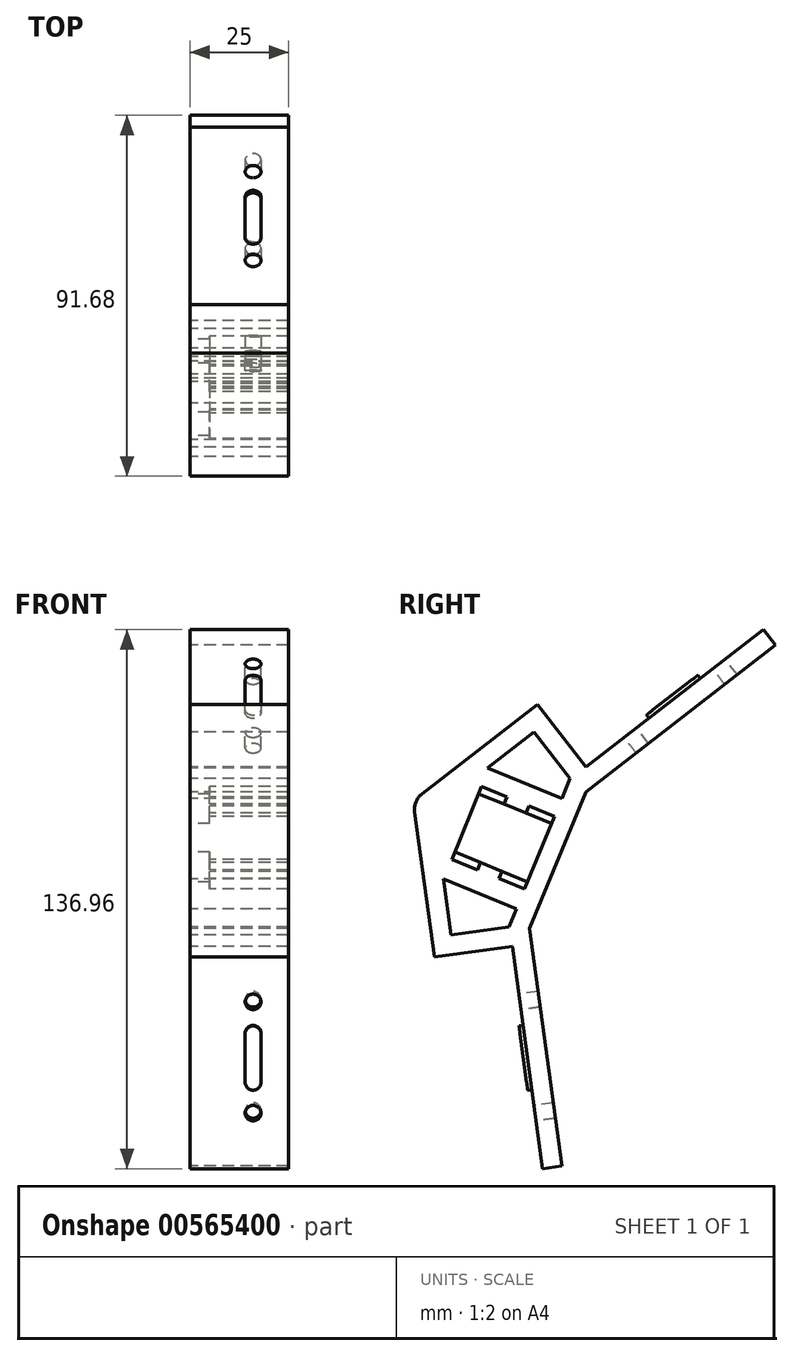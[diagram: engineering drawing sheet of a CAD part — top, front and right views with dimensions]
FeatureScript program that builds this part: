
annotation { "Feature Type Name" : "Feature", "Feature Type Description" : "" }
export const myFeature = defineFeature(function(context is Context, id is Id, definition is map)
    precondition{}
    {
        {
            var Q0;
            Q0=qCreatedBy(makeId("Right.planeOp"),FACE);
            var sketch = newSketch(context, id + "F0", { "sketchPlane" : qUnion([Q0])});
            skLineSegment(sketch, "E0", {"start": v(-33.6, 14.18) * mm, "end": v(-1.95, 38.65) * mm});
            skLineSegment(sketch, "E1", {"start": v(-1.95, 38.65) * mm, "end": v(10.28, 22.83) * mm});
            skLineSegment(sketch, "E2", {"start": v(-8.4, -22.77) * mm, "end": v(-28.23, -25.46) * mm});
            skLineSegment(sketch, "E3", {"start": v(-28.23, -25.46) * mm, "end": v(-33.6, 14.18) * mm});
            skLineSegment(sketch, "E4", {"start": v(10.28, 22.83) * mm, "end": v(55.37, 57.7) * mm});
            skLineSegment(sketch, "E5", {"start": v(55.37, 57.7) * mm, "end": v(58.43, 53.74) * mm});
            skLineSegment(sketch, "E6", {"start": v(58.43, 53.74) * mm, "end": v(10.28, 16.5) * mm});
            skLineSegment(sketch, "E7", {"start": v(10.28, 16.5) * mm, "end": v(-3.97, -18.27) * mm});
            skLineSegment(sketch, "E8", {"start": v(-3.97, -18.27) * mm, "end": v(4.2, -78.59) * mm});
            skLineSegment(sketch, "E9", {"start": v(4.2, -78.59) * mm, "end": v(-0.75, -79.26) * mm});
            skLineSegment(sketch, "E10", {"start": v(-0.75, -79.26) * mm, "end": v(-8.4, -22.77) * mm});
            skPoint(sketch, "E11", {"position": v(34.35, 35.12) * mm});
            skPoint(sketch, "E12", {"position": v(0.11, -48.43) * mm});
            skLineSegment(sketch, "E13", {"start": v(2.32, 10.27) * mm, "end": v(-16.19, 17.85) * mm});
            skLineSegment(sketch, "E14", {"start": v(-16.19, 17.85) * mm, "end": v(-23.77, -0.65) * mm});
            skLineSegment(sketch, "E15", {"start": v(-23.77, -0.65) * mm, "end": v(-5.26, -8.24) * mm});
            skLineSegment(sketch, "E16", {"start": v(-5.26, -8.24) * mm, "end": v(2.32, 10.27) * mm});
            skPoint(sketch, "E17", {"position": v(3.15, -0.88) * mm});
            skPoint(sketch, "E18", {"position": v(-1.47, 1.01) * mm});
            skLineSegment(sketch, "E19", {"start": v(3.15, -0.88) * mm, "end": v(-1.47, 1.01) * mm});
            skLineSegment(sketch, "E20", {"start": v(1.56, 8.42) * mm, "end": v(-16.94, 16) * mm});
            skLineSegment(sketch, "E21", {"start": v(-4.5, -6.39) * mm, "end": v(-23.01, 1.2) * mm});
            skLineSegment(sketch, "E22", {"start": v(-11.74, -5.58) * mm, "end": v(-10.98, -3.73) * mm});
            skLineSegment(sketch, "E23", {"start": v(-17.3, -3.3) * mm, "end": v(-16.53, -1.46) * mm});
            skLineSegment(sketch, "E24", {"start": v(-10.47, 13.35) * mm, "end": v(-9.7, 15.2) * mm});
            skPoint(sketch, "E25", {"position": v(-14.52, -4.45) * mm});
            skPoint(sketch, "E26", {"position": v(-6.93, 14.06) * mm});
            skLineSegment(sketch, "E27", {"start": v(-4.92, 11.07) * mm, "end": v(-4.16, 12.92) * mm});
            skLineSegment(sketch, "E28", {"start": v(-2.85, 31.63) * mm, "end": v(6.25, 19.86) * mm});
            skLineSegment(sketch, "E29", {"start": v(6.25, 19.86) * mm, "end": v(4.17, 14.8) * mm});
            skLineSegment(sketch, "E30", {"start": v(4.17, 14.8) * mm, "end": v(-14.65, 22.5) * mm});
            skLineSegment(sketch, "E31", {"start": v(-14.65, 22.5) * mm, "end": v(-2.85, 31.63) * mm});
            skLineSegment(sketch, "E32", {"start": v(-7.31, -13.24) * mm, "end": v(-9.2, -17.83) * mm});
            skLineSegment(sketch, "E33", {"start": v(-9.2, -17.83) * mm, "end": v(-23.94, -19.83) * mm});
            skLineSegment(sketch, "E34", {"start": v(-23.94, -19.83) * mm, "end": v(-25.87, -5.64) * mm});
            skPoint(sketch, "E34.endSnap0", {"position": v(-30.91, -5.64) * mm});
            skLineSegment(sketch, "E35", {"start": v(-25.87, -5.64) * mm, "end": v(-7.31, -13.24) * mm});
            skSolve(sketch);
        }
        {
            var Q0;
            Q0=makeQuery(id+"F0.imprint","IMPRINT",FACE,{"disambiguationData":[TD([[makeQuery(id+"F0.imprint","IMPRINT",EDGE,{"derivedFrom":sQuery(id+"F0.wireOp",EDGE,"E0")}),-1.0]])]});
            var Q1;
            {var subQ0=sQuery(id+"F0.wireOp",EDGE,"E22");Q1=makeQuery(id+"F0.imprint","IMPRINT",FACE,{"disambiguationData":[TD([[makeQuery(id+"F0.imprint","IMPRINT",EDGE,{"derivedFrom":subQ0}),1.0]])]});}
            var Q2;
            {var subQ0=sQuery(id+"F0.wireOp",EDGE,"E24");Q2=makeQuery(id+"F0.imprint","IMPRINT",FACE,{"disambiguationData":[TD([[makeQuery(id+"F0.imprint","IMPRINT",EDGE,{"derivedFrom":subQ0}),-1.0]])]});}
            extrude(context, id + "F1", {"entities" : qUnion([Q0, Q1, Q2]), "depth" : 25 * mm, "offsetDistance" : 25 * mm});
        }
        {
            var Q0;
            {var subQ3=sQuery(id+"F0.wireOp",EDGE,"E22");Q0=makeQuery(id+"F0.imprint","IMPRINT",FACE,{"disambiguationData":[TD([[makeQuery(id+"F0.imprint","IMPRINT",EDGE,{"derivedFrom":subQ3}),-1.0]])]});}
            var Q1;
            {var subQ5=sQuery(id+"F0.wireOp",EDGE,"E23");Q1=makeQuery(id+"F0.imprint","IMPRINT",FACE,{"disambiguationData":[TD([[makeQuery(id+"F0.imprint","IMPRINT",EDGE,{"derivedFrom":subQ5}),1.0]])]});}
            var Q2;
            {var subQ3=sQuery(id+"F0.wireOp",EDGE,"E24");Q2=makeQuery(id+"F0.imprint","IMPRINT",FACE,{"disambiguationData":[TD([[makeQuery(id+"F0.imprint","IMPRINT",EDGE,{"derivedFrom":subQ3}),1.0]])]});}
            var Q3;
            {var subQ3=sQuery(id+"F0.wireOp",EDGE,"E27");Q3=makeQuery(id+"F0.imprint","IMPRINT",FACE,{"disambiguationData":[TD([[makeQuery(id+"F0.imprint","IMPRINT",EDGE,{"derivedFrom":subQ3}),-1.0]])]});}
            extrude(context, id + "F2", {"entities" : qUnion([Q0, Q1, Q2, Q3]), "operationType" : NewBodyOperationType.ADD, "depth" : 5 * mm, "offsetDistance" : 25 * mm});
        }
        {
            var Q0;
            Q0=makeQuery(id+"F1.opExtrude","SWEPT_EDGE",EDGE,{"disambiguationData":[OSD([sQuery(id+"F0.wireOp",EDGE,"E0"),sQuery(id+"F0.wireOp",EDGE,"E3")])]});
            fillet(context, id + "F3", {"entities" : qUnion([Q0]), "radius" : 5 * mm, "tangentPropagation" : true, "allowEdgeOverflow" : false});
        }
        {
            var Q0;
            Q0=makeQuery(id+"F1.opExtrude","SWEPT_FACE",FACE,{"disambiguationData":[OSD([sQuery(id+"F0.wireOp",EDGE,"E4")])]});
            var sketch = newSketch(context, id + "F4", { "sketchPlane" : qUnion([Q0])});
            skCircle(sketch, "E36", {"center": v(16, 56.85) * mm, "radius": 2 * mm});
            skCircle(sketch, "E37", {"center": v(16, 44.35) * mm, "radius": 2 * mm});
            skLineSegment(sketch, "E38", {"start": v(18, 56.85) * mm, "end": v(18, 44.35) * mm});
            skLineSegment(sketch, "E39", {"start": v(14, 44.35) * mm, "end": v(14, 56.85) * mm});
            skCircle(sketch, "E40", {"center": v(16, 64.85) * mm, "radius": 2 * mm});
            skCircle(sketch, "E41", {"center": v(16, 36.35) * mm, "radius": 2 * mm});
            skLineSegment(sketch, "E42", {"start": v(18, 56.85) * mm, "end": v(18, 64.85) * mm});
            skLineSegment(sketch, "E43", {"start": v(14, 64.85) * mm, "end": v(14, 56.85) * mm});
            skLineSegment(sketch, "E44", {"start": v(18, 44.35) * mm, "end": v(18, 36.35) * mm});
            skLineSegment(sketch, "E45", {"start": v(14, 44.35) * mm, "end": v(14, 36.35) * mm});
            skSolve(sketch);
        }
        {
            var Q0;
            {var subQ0=sQuery(id+"F4.wireOp",EDGE,"E36");var subQ1=makeQuery(id+"F4.imprint","INTERSECT",VERTEX,{"derivedFrom":[subQ0,sQuery(id+"F4.wireOp",EDGE,"E38")]});Q0=makeQuery(id+"F4.imprint","IMPRINT",FACE,{"disambiguationData":[TD([[makeQuery(id+"F4.imprint","IMPRINT",EDGE,{"disambiguationData":[TD([[subQ1,-1.0]])],"derivedFrom":subQ0}),1.0]])]});}
            var Q1;
            {var subQ0=sQuery(id+"F4.wireOp",EDGE,"E37");var subQ1=makeQuery(id+"F4.imprint","INTERSECT",VERTEX,{"derivedFrom":[subQ0,sQuery(id+"F4.wireOp",EDGE,"E38")]});Q1=makeQuery(id+"F4.imprint","IMPRINT",FACE,{"disambiguationData":[TD([[makeQuery(id+"F4.imprint","IMPRINT",EDGE,{"disambiguationData":[TD([[subQ1,1.0]])],"derivedFrom":subQ0}),1.0]])]});}
            var Q2;
            {var subQ0=sQuery(id+"F4.wireOp",EDGE,"E38");Q2=makeQuery(id+"F4.imprint","IMPRINT",FACE,{"disambiguationData":[TD([[makeQuery(id+"F4.imprint","IMPRINT",EDGE,{"derivedFrom":subQ0}),-1.0]])]});}
            extrude(context, id + "F5", {"entities" : qUnion([Q0, Q1, Q2]), "operationType" : NewBodyOperationType.ADD, "depth" : 1 * mm, "offsetDistance" : 25 * mm});
        }
        {
            var Q0;
            {var subQ0=sQuery(id+"F4.wireOp",EDGE,"E40");var subQ1=makeQuery(id+"F4.imprint","INTERSECT",VERTEX,{"derivedFrom":[subQ0,sQuery(id+"F4.wireOp",EDGE,"E42")]});Q0=makeQuery(id+"F4.imprint","IMPRINT",FACE,{"disambiguationData":[TD([[makeQuery(id+"F4.imprint","IMPRINT",EDGE,{"disambiguationData":[TD([[subQ1,-1.0]])],"derivedFrom":subQ0}),1.0]])]});}
            var Q1;
            {var subQ0=sQuery(id+"F4.wireOp",EDGE,"E41");var subQ1=makeQuery(id+"F4.imprint","INTERSECT",VERTEX,{"derivedFrom":[subQ0,sQuery(id+"F4.wireOp",EDGE,"E44")]});Q1=makeQuery(id+"F4.imprint","IMPRINT",FACE,{"disambiguationData":[TD([[makeQuery(id+"F4.imprint","IMPRINT",EDGE,{"disambiguationData":[TD([[subQ1,-1.0]])],"derivedFrom":subQ0}),1.0]])]});}
            extrude(context, id + "F6", {"entities" : qUnion([Q0, Q1]), "operationType" : NewBodyOperationType.REMOVE, "oppositeDirection" : true, "depth" : 5 * mm, "offsetDistance" : 25 * mm});
        }
        {
            var Q0;
            Q0=makeQuery(id+"F1.opExtrude","SWEPT_FACE",FACE,{"disambiguationData":[OSD([sQuery(id+"F0.wireOp",EDGE,"E10")])]});
            var sketch = newSketch(context, id + "F7", { "sketchPlane" : qUnion([Q0])});
            skCircle(sketch, "E46", {"center": v(16, -35.69) * mm, "radius": 2 * mm});
            skCircle(sketch, "E47", {"center": v(16, -43.69) * mm, "radius": 2 * mm});
            skCircle(sketch, "E48", {"center": v(16, -56.19) * mm, "radius": 2 * mm});
            skCircle(sketch, "E49", {"center": v(16, -64.19) * mm, "radius": 2 * mm});
            skLineSegment(sketch, "E50", {"start": v(18, -35.69) * mm, "end": v(18, -43.69) * mm});
            skLineSegment(sketch, "E51", {"start": v(18, -43.69) * mm, "end": v(18, -56.19) * mm});
            skLineSegment(sketch, "E52", {"start": v(18, -64.19) * mm, "end": v(18, -56.19) * mm});
            skLineSegment(sketch, "E53", {"start": v(14, -35.69) * mm, "end": v(14, -43.69) * mm});
            skLineSegment(sketch, "E54", {"start": v(14, -43.69) * mm, "end": v(14, -56.19) * mm});
            skLineSegment(sketch, "E55", {"start": v(14, -56.19) * mm, "end": v(14, -64.19) * mm});
            skSolve(sketch);
        }
        {
            var Q0;
            {var subQ0=sQuery(id+"F7.wireOp",EDGE,"E47");var subQ1=makeQuery(id+"F7.imprint","INTERSECT",VERTEX,{"derivedFrom":[subQ0,sQuery(id+"F7.wireOp",EDGE,"E50"),sQuery(id+"F7.wireOp",EDGE,"E51")]});Q0=makeQuery(id+"F7.imprint","IMPRINT",FACE,{"disambiguationData":[TD([[makeQuery(id+"F7.imprint","IMPRINT",EDGE,{"disambiguationData":[TD([[subQ1,-1.0]])],"derivedFrom":subQ0}),1.0]])]});}
            var Q1;
            {var subQ0=sQuery(id+"F7.wireOp",EDGE,"E51");Q1=makeQuery(id+"F7.imprint","IMPRINT",FACE,{"disambiguationData":[TD([[makeQuery(id+"F7.imprint","IMPRINT",EDGE,{"derivedFrom":subQ0}),-1.0]])]});}
            var Q2;
            {var subQ0=sQuery(id+"F7.wireOp",EDGE,"E48");var subQ1=makeQuery(id+"F7.imprint","INTERSECT",VERTEX,{"derivedFrom":[subQ0,sQuery(id+"F7.wireOp",EDGE,"E51"),sQuery(id+"F7.wireOp",EDGE,"E52")]});Q2=makeQuery(id+"F7.imprint","IMPRINT",FACE,{"disambiguationData":[TD([[makeQuery(id+"F7.imprint","IMPRINT",EDGE,{"disambiguationData":[TD([[subQ1,-1.0]])],"derivedFrom":subQ0}),1.0]])]});}
            extrude(context, id + "F8", {"entities" : qUnion([Q0, Q1, Q2]), "operationType" : NewBodyOperationType.ADD, "depth" : 1 * mm, "offsetDistance" : 25 * mm});
        }
        {
            var Q0;
            {var subQ0=sQuery(id+"F7.wireOp",EDGE,"E46");var subQ1=makeQuery(id+"F7.imprint","INTERSECT",VERTEX,{"derivedFrom":[subQ0,sQuery(id+"F7.wireOp",EDGE,"E50")]});Q0=makeQuery(id+"F7.imprint","IMPRINT",FACE,{"disambiguationData":[TD([[makeQuery(id+"F7.imprint","IMPRINT",EDGE,{"disambiguationData":[TD([[subQ1,1.0]])],"derivedFrom":subQ0}),1.0]])]});}
            var Q1;
            {var subQ0=sQuery(id+"F7.wireOp",EDGE,"E49");var subQ1=makeQuery(id+"F7.imprint","INTERSECT",VERTEX,{"derivedFrom":[subQ0,sQuery(id+"F7.wireOp",EDGE,"E52")]});Q1=makeQuery(id+"F7.imprint","IMPRINT",FACE,{"disambiguationData":[TD([[makeQuery(id+"F7.imprint","IMPRINT",EDGE,{"disambiguationData":[TD([[subQ1,-1.0]])],"derivedFrom":subQ0}),1.0]])]});}
            extrude(context, id + "F9", {"entities" : qUnion([Q0, Q1]), "operationType" : NewBodyOperationType.REMOVE, "oppositeDirection" : true, "depth" : 5 * mm, "offsetDistance" : 25 * mm});
        }
    });
